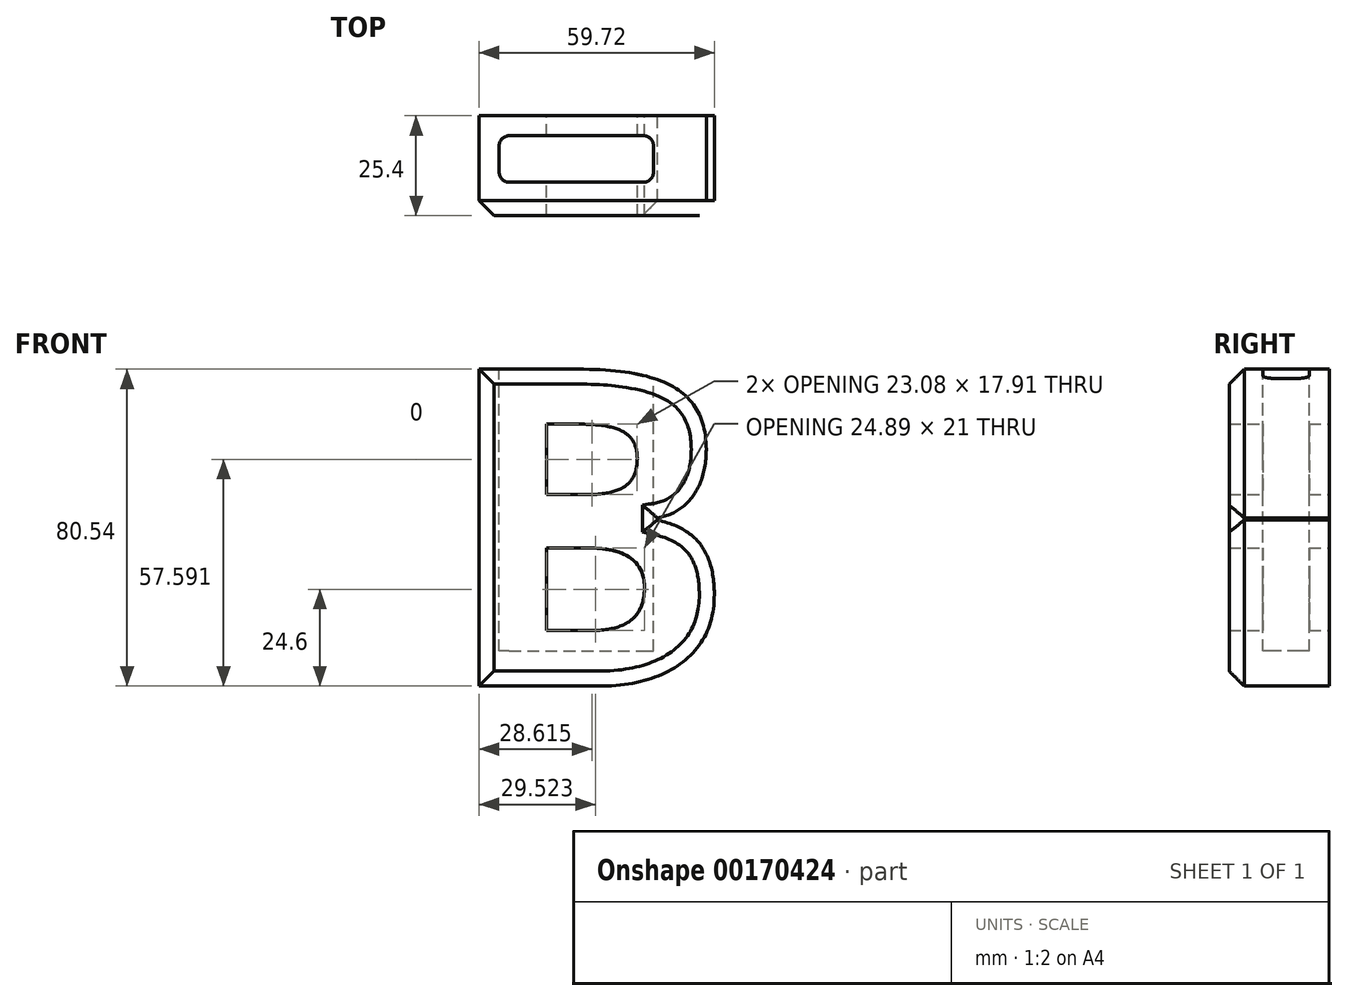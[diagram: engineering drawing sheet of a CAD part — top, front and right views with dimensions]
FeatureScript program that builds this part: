
annotation { "Feature Type Name" : "Feature", "Feature Type Description" : "" }
export const myFeature = defineFeature(function(context is Context, id is Id, definition is map)
    precondition{}
    {
        {
            var Q0;
            Q0=qCreatedBy(makeId("Front.planeOp"),FACE);
            var sketch = newSketch(context, id + "F0", { "sketchPlane" : qUnion([Q0])});
            skText(sketch, "E0", { "text": "B", "fontName": "OpenSans-Bold.ttf"});
            const initialGuessF0  = {"E0": [0, 0, 1, 0, 0.08123]};
            skSetInitialGuess(sketch, initialGuessF0);
            skSolve(sketch);
        }
        {
            var Q0;
            Q0=makeQuery(id+"F0.imprint","IMPRINT",FACE,{"disambiguationData":[TD([[makeQuery(id+"F0.imprint","IMPRINT",EDGE,{"derivedFrom":sQuery(id+"F0.wireOp",EDGE,"E0.sketch_text.stroke-0")}),-1.0]])]});
            extrude(context, id + "F1", {"entities" : qUnion([Q0]), "depth" : 25.4 * mm});
        }
        {
            var Q0;
            Q0=makeQuery(id+"F1.opExtrude","CAP_EDGE",EDGE,{"disambiguationData":[OSD([sQuery(id+"F0.wireOp",EDGE,"E0.sketch_text.stroke-0")])],"isStart":false});
            var Q1;
            Q1=makeQuery(id+"F1.opExtrude","CAP_EDGE",EDGE,{"disambiguationData":[OSD([sQuery(id+"F0.wireOp",EDGE,"E0.sketch_text.stroke-6")])],"isStart":false});
            var Q2;
            Q2=makeQuery(id+"F1.opExtrude","CAP_EDGE",EDGE,{"disambiguationData":[OSD([sQuery(id+"F0.wireOp",EDGE,"E0.sketch_text.stroke-11")])],"isStart":false});
            var Q3;
            Q3=makeQuery(id+"F1.opExtrude","CAP_EDGE",EDGE,{"disambiguationData":[OSD([sQuery(id+"F0.wireOp",EDGE,"E0.sketch_text.stroke-5")])],"isStart":false});
            chamfer(context, id + "F2", {"entities" : qUnion([Q0, Q1, Q2, Q3]), "width" : 3.8 * mm, "tangentPropagation" : true});
        }
        {
            var Q0;
            Q0=makeQuery(id+"F1.opExtrude","SWEPT_FACE",FACE,{"disambiguationData":[OSD([sQuery(id+"F0.wireOp",EDGE,"E0.sketch_text.stroke-0")])]});
            var sketch = newSketch(context, id + "F3", { "sketchPlane" : qUnion([Q0])});
            skLineSegment(sketch, "E1.bottom", {"start": v(17.76, -5.08) * mm, "end": v(51.86, -5.08) * mm});
            skLineSegment(sketch, "E1.top", {"start": v(17.76, -16.93) * mm, "end": v(51.86, -16.93) * mm});
            skLineSegment(sketch, "E1.left", {"start": v(15.22, -7.62) * mm, "end": v(15.22, -14.39) * mm});
            skLineSegment(sketch, "E1.right", {"start": v(54.4, -7.62) * mm, "end": v(54.4, -14.39) * mm});
            skPoint(sketch, "E2.visualSharp", {"position": v(15.22, -5.08) * mm});
            skArc(sketch, "E2.filletArc", {"start": v(17.76, -5.08) * mm, "mid": v(15.96, -5.82) * mm, "end": v(15.22, -7.62) * mm});
            skPoint(sketch, "E3.visualSharp", {"position": v(15.22, -16.93) * mm});
            skArc(sketch, "E3.filletArc", {"start": v(15.22, -14.39) * mm, "mid": v(15.96, -16.18) * mm, "end": v(17.76, -16.93) * mm});
            skPoint(sketch, "E4.visualSharp", {"position": v(54.4, -16.93) * mm});
            skArc(sketch, "E4.filletArc", {"start": v(51.86, -16.93) * mm, "mid": v(53.66, -16.18) * mm, "end": v(54.4, -14.39) * mm});
            skPoint(sketch, "E5.visualSharp", {"position": v(54.4, -5.08) * mm});
            skArc(sketch, "E5.filletArc", {"start": v(54.4, -7.62) * mm, "mid": v(53.66, -5.82) * mm, "end": v(51.86, -5.08) * mm});
            skSolve(sketch);
        }
        {
            var Q0;
            Q0=makeQuery(id+"F3.imprint","IMPRINT",FACE,{"disambiguationData":[TD([[makeQuery(id+"F3.imprint","IMPRINT",EDGE,{"derivedFrom":sQuery(id+"F3.wireOp",EDGE,"E1.left")}),1.0]])]});
            var Q1;
            Q1=makeQuery(id+"F3.imprint","IMPRINT",FACE,{"disambiguationData":[TD([[makeQuery(id+"F3.imprint","IMPRINT",EDGE,{"derivedFrom":sQuery(id+"F3.wireOp",EDGE,"E1.right")}),-1.0]])]});
            extrude(context, id + "F4", {"entities" : qUnion([Q0, Q1]), "operationType" : NewBodyOperationType.REMOVE, "oppositeDirection" : true, "depth" : 71.63 * mm});
        }
    });
